# Revit family: Versailles 400
name_source: partatom
category: Lighting Fixtures
revit_build: Autodesk Revit 2018 (Build: 20170223_1515(x64)
units: mm (PartAtom-declared; Revit-internal decimal feet)

## family parameters
Always vertical = Yes
Cut with Voids When Loaded = No
Host = Wall
Light Source = Yes
OmniClass Number = 23.80.70.00
OmniClass Title = Lighting
Part Type = Normal
Room Calculation Point = No
Round Connector Dimension = Use Diameter
Shared = No

## types (3) — shared parameters
Color Filter = 16777215
Colour Temperature = 3000 K
Dimmable = No
Dimming Lamp Color Temperature Shift = <None>
Dimming Method = None
Driver Included = Yes
Driver Required = No
Efficacy (lm/w) = 89.04
Electrical Class = 2
Emit from Line Length = 500 mm  [stored 1.64042 ft]
Lamp = LED
Light Source Fixed = Yes
Location rating = IP44
Luminous Flux = 650 lm
Main Material = Metal - Steel
Manufacturer = Astro Lighting Ltd
Model = Versailles 250
Photometric Web File = GNC-21390 Versailles 400 LED - 7838.ies
Power (Watts) = 7.3
Product Location = Bathroom/Indoor
Tilt Angle = 0.00°
URL = www.astrolighting.com

## per-type parameters (varying)
| type | Main Finish | Product Name | Product SKU |
| Astro Versaiiles 400 Polished Chrome 1380002 | Polished Chrome | Versailles 400 Chrome | 1380002 |
| Astro Versailles 400 Bronze 1380003 | Bronze | Versailles 400 Bronze | 1380003 |
| Astro Versailles 400 Matt Gold 1380016 | Matt Gold | Versailles 400 Gold | 1380016 |

note: [stored X ft] marks values corroborated as IEEE doubles in the binary element streams (Revit-internal decimal feet)

## geometry (parser evidence)
native form markers: Sweep x1
no freeform markers — native parametric forms only
